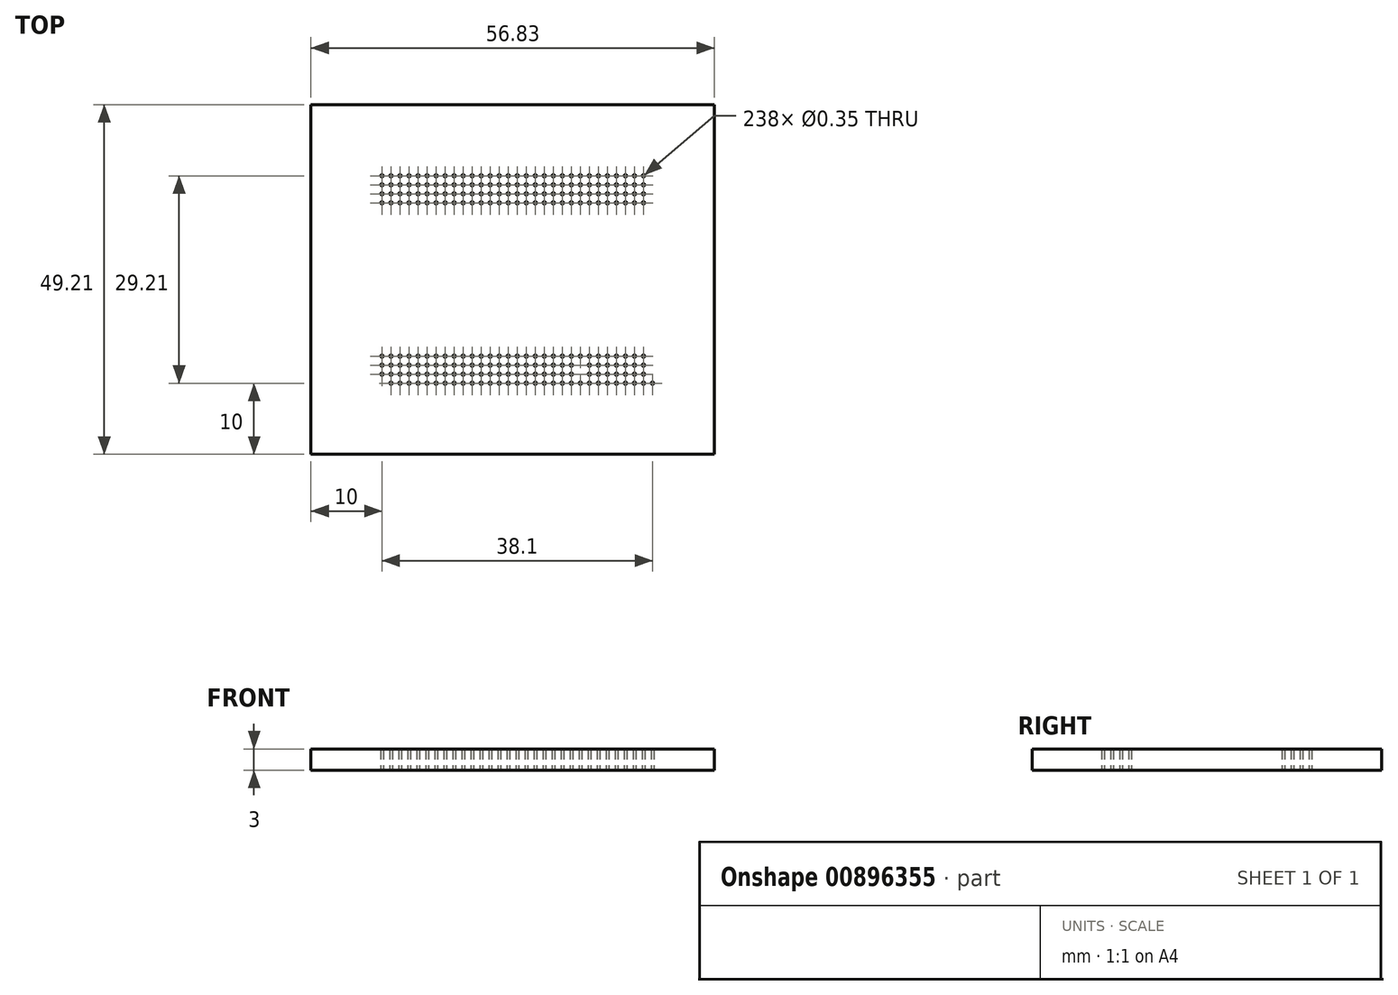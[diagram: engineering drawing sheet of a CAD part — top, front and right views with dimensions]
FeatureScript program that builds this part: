
annotation { "Feature Type Name" : "Feature", "Feature Type Description" : "" }
export const myFeature = defineFeature(function(context is Context, id is Id, definition is map)
    precondition{}
    {
        {
            var Q0;
            Q0=qCreatedBy(makeId("Top.planeOp"),FACE);
            var sketch = newSketch(context, id + "F0", { "sketchPlane" : qUnion([Q0])});
            skLineSegment(sketch, "E0.bottom", {"start": v(0, 0) * mm, "end": v(-56.83, 0) * mm});
            skLineSegment(sketch, "E0.top", {"start": v(0, 49.2) * mm, "end": v(-56.83, 49.2) * mm});
            skLineSegment(sketch, "E0.left", {"start": v(0, 0) * mm, "end": v(0, 49.2) * mm});
            skLineSegment(sketch, "E0.right", {"start": v(-56.83, 0) * mm, "end": v(-56.83, 49.2) * mm});
            skCircle(sketch, "E1", {"center": v(-46.83, 10) * mm, "radius": 0.18 * mm});
            skLineSegment(sketch, "E2", {"start": v(-46.83, 10) * mm, "end": v(-46.83, 10.4) * mm, "construction": true});
            skCircle(sketch, "E3", {"center": v(-46.83, 11.27) * mm, "radius": 0.17 * mm});
            skCircle(sketch, "E4", {"center": v(-46.83, 12.54) * mm, "radius": 0.17 * mm});
            skCircle(sketch, "E5", {"center": v(-46.83, 13.8) * mm, "radius": 0.17 * mm});
            skCircle(sketch, "E6.0.1.0", {"center": v(-46.83, 39.2) * mm, "radius": 0.17 * mm});
            skCircle(sketch, "E6.0.1.1", {"center": v(-46.83, 37.94) * mm, "radius": 0.17 * mm});
            skCircle(sketch, "E6.0.1.2", {"center": v(-46.83, 36.67) * mm, "radius": 0.17 * mm});
            skCircle(sketch, "E6.0.1.3", {"center": v(-46.83, 35.4) * mm, "radius": 0.18 * mm});
            skCircle(sketch, "E6.1.0.0", {"center": v(-45.56, 13.8) * mm, "radius": 0.17 * mm});
            skCircle(sketch, "E6.1.0.1", {"center": v(-45.56, 12.54) * mm, "radius": 0.17 * mm});
            skCircle(sketch, "E6.1.0.2", {"center": v(-45.56, 11.27) * mm, "radius": 0.17 * mm});
            skCircle(sketch, "E6.1.0.3", {"center": v(-45.56, 10) * mm, "radius": 0.18 * mm});
            skCircle(sketch, "E6.1.1.0", {"center": v(-45.56, 39.2) * mm, "radius": 0.17 * mm});
            skCircle(sketch, "E6.1.1.1", {"center": v(-45.56, 37.94) * mm, "radius": 0.17 * mm});
            skCircle(sketch, "E6.1.1.2", {"center": v(-45.56, 36.67) * mm, "radius": 0.17 * mm});
            skCircle(sketch, "E6.1.1.3", {"center": v(-45.56, 35.4) * mm, "radius": 0.18 * mm});
            skCircle(sketch, "E6.2.0.0", {"center": v(-44.3, 13.8) * mm, "radius": 0.17 * mm});
            skCircle(sketch, "E6.2.0.1", {"center": v(-44.3, 12.54) * mm, "radius": 0.17 * mm});
            skCircle(sketch, "E6.2.0.2", {"center": v(-44.3, 11.27) * mm, "radius": 0.17 * mm});
            skCircle(sketch, "E6.2.0.3", {"center": v(-44.3, 10) * mm, "radius": 0.18 * mm});
            skCircle(sketch, "E6.2.1.0", {"center": v(-44.3, 39.2) * mm, "radius": 0.17 * mm});
            skCircle(sketch, "E6.2.1.1", {"center": v(-44.3, 37.94) * mm, "radius": 0.17 * mm});
            skCircle(sketch, "E6.2.1.2", {"center": v(-44.3, 36.67) * mm, "radius": 0.17 * mm});
            skCircle(sketch, "E6.2.1.3", {"center": v(-44.3, 35.4) * mm, "radius": 0.18 * mm});
            skCircle(sketch, "E6.3.0.0", {"center": v(-43.02, 13.8) * mm, "radius": 0.17 * mm});
            skCircle(sketch, "E6.3.0.1", {"center": v(-43.02, 12.54) * mm, "radius": 0.17 * mm});
            skCircle(sketch, "E6.3.0.2", {"center": v(-43.02, 11.27) * mm, "radius": 0.17 * mm});
            skCircle(sketch, "E6.3.0.3", {"center": v(-43.02, 10) * mm, "radius": 0.18 * mm});
            skCircle(sketch, "E6.3.1.0", {"center": v(-43.02, 39.2) * mm, "radius": 0.17 * mm});
            skCircle(sketch, "E6.3.1.1", {"center": v(-43.02, 37.94) * mm, "radius": 0.17 * mm});
            skCircle(sketch, "E6.3.1.2", {"center": v(-43.02, 36.67) * mm, "radius": 0.17 * mm});
            skCircle(sketch, "E6.3.1.3", {"center": v(-43.02, 35.4) * mm, "radius": 0.18 * mm});
            skCircle(sketch, "E6.4.0.0", {"center": v(-41.75, 13.8) * mm, "radius": 0.17 * mm});
            skCircle(sketch, "E6.4.0.1", {"center": v(-41.75, 12.54) * mm, "radius": 0.17 * mm});
            skCircle(sketch, "E6.4.0.2", {"center": v(-41.75, 11.27) * mm, "radius": 0.17 * mm});
            skCircle(sketch, "E6.4.0.3", {"center": v(-41.75, 10) * mm, "radius": 0.18 * mm});
            skCircle(sketch, "E6.4.1.0", {"center": v(-41.75, 39.2) * mm, "radius": 0.17 * mm});
            skCircle(sketch, "E6.4.1.1", {"center": v(-41.75, 37.94) * mm, "radius": 0.17 * mm});
            skCircle(sketch, "E6.4.1.2", {"center": v(-41.75, 36.67) * mm, "radius": 0.17 * mm});
            skCircle(sketch, "E6.4.1.3", {"center": v(-41.75, 35.4) * mm, "radius": 0.18 * mm});
            skCircle(sketch, "E6.5.0.0", {"center": v(-40.48, 13.8) * mm, "radius": 0.17 * mm});
            skCircle(sketch, "E6.5.0.1", {"center": v(-40.48, 12.54) * mm, "radius": 0.17 * mm});
            skCircle(sketch, "E6.5.0.2", {"center": v(-40.48, 11.27) * mm, "radius": 0.17 * mm});
            skCircle(sketch, "E6.5.0.3", {"center": v(-40.48, 10) * mm, "radius": 0.18 * mm});
            skCircle(sketch, "E6.5.1.0", {"center": v(-40.48, 39.2) * mm, "radius": 0.17 * mm});
            skCircle(sketch, "E6.5.1.1", {"center": v(-40.48, 37.94) * mm, "radius": 0.17 * mm});
            skCircle(sketch, "E6.5.1.2", {"center": v(-40.48, 36.67) * mm, "radius": 0.17 * mm});
            skCircle(sketch, "E6.5.1.3", {"center": v(-40.48, 35.4) * mm, "radius": 0.18 * mm});
            skCircle(sketch, "E6.6.0.0", {"center": v(-39.21, 13.8) * mm, "radius": 0.17 * mm});
            skCircle(sketch, "E6.6.0.1", {"center": v(-39.21, 12.54) * mm, "radius": 0.17 * mm});
            skCircle(sketch, "E6.6.0.2", {"center": v(-39.21, 11.27) * mm, "radius": 0.17 * mm});
            skCircle(sketch, "E6.6.0.3", {"center": v(-39.21, 10) * mm, "radius": 0.18 * mm});
            skCircle(sketch, "E6.6.1.0", {"center": v(-39.21, 39.2) * mm, "radius": 0.17 * mm});
            skCircle(sketch, "E6.6.1.1", {"center": v(-39.21, 37.94) * mm, "radius": 0.17 * mm});
            skCircle(sketch, "E6.6.1.2", {"center": v(-39.21, 36.67) * mm, "radius": 0.17 * mm});
            skCircle(sketch, "E6.6.1.3", {"center": v(-39.21, 35.4) * mm, "radius": 0.18 * mm});
            skCircle(sketch, "E6.7.0.0", {"center": v(-37.94, 13.8) * mm, "radius": 0.17 * mm});
            skCircle(sketch, "E6.7.0.3", {"center": v(-37.94, 10) * mm, "radius": 0.18 * mm});
            skCircle(sketch, "E6.7.1.0", {"center": v(-37.94, 39.2) * mm, "radius": 0.17 * mm});
            skCircle(sketch, "E6.7.1.1", {"center": v(-37.94, 37.94) * mm, "radius": 0.17 * mm});
            skCircle(sketch, "E6.7.1.2", {"center": v(-37.94, 36.67) * mm, "radius": 0.17 * mm});
            skCircle(sketch, "E6.7.1.3", {"center": v(-37.94, 35.4) * mm, "radius": 0.18 * mm});
            skCircle(sketch, "E6.8.0.0", {"center": v(-36.67, 13.8) * mm, "radius": 0.17 * mm});
            skCircle(sketch, "E6.8.0.1", {"center": v(-36.67, 12.54) * mm, "radius": 0.17 * mm});
            skCircle(sketch, "E6.8.0.2", {"center": v(-36.67, 11.27) * mm, "radius": 0.17 * mm});
            skCircle(sketch, "E6.8.0.3", {"center": v(-36.67, 10) * mm, "radius": 0.18 * mm});
            skCircle(sketch, "E6.8.1.0", {"center": v(-36.67, 39.2) * mm, "radius": 0.17 * mm});
            skCircle(sketch, "E6.8.1.1", {"center": v(-36.67, 37.94) * mm, "radius": 0.17 * mm});
            skCircle(sketch, "E6.8.1.2", {"center": v(-36.67, 36.67) * mm, "radius": 0.17 * mm});
            skCircle(sketch, "E6.8.1.3", {"center": v(-36.67, 35.4) * mm, "radius": 0.18 * mm});
            skCircle(sketch, "E6.9.0.0", {"center": v(-35.4, 13.8) * mm, "radius": 0.17 * mm});
            skCircle(sketch, "E6.9.0.1", {"center": v(-35.4, 12.54) * mm, "radius": 0.17 * mm});
            skCircle(sketch, "E6.9.0.2", {"center": v(-35.4, 11.27) * mm, "radius": 0.17 * mm});
            skCircle(sketch, "E6.9.0.3", {"center": v(-35.4, 10) * mm, "radius": 0.18 * mm});
            skCircle(sketch, "E6.9.1.0", {"center": v(-35.4, 39.2) * mm, "radius": 0.17 * mm});
            skCircle(sketch, "E6.9.1.1", {"center": v(-35.4, 37.94) * mm, "radius": 0.17 * mm});
            skCircle(sketch, "E6.9.1.2", {"center": v(-35.4, 36.67) * mm, "radius": 0.17 * mm});
            skCircle(sketch, "E6.9.1.3", {"center": v(-35.4, 35.4) * mm, "radius": 0.18 * mm});
            skCircle(sketch, "E6.10.0.0", {"center": v(-34.13, 13.8) * mm, "radius": 0.17 * mm});
            skCircle(sketch, "E6.10.0.1", {"center": v(-34.13, 12.54) * mm, "radius": 0.17 * mm});
            skCircle(sketch, "E6.10.0.2", {"center": v(-34.13, 11.27) * mm, "radius": 0.17 * mm});
            skCircle(sketch, "E6.10.0.3", {"center": v(-34.13, 10) * mm, "radius": 0.18 * mm});
            skCircle(sketch, "E6.10.1.0", {"center": v(-34.13, 39.2) * mm, "radius": 0.17 * mm});
            skCircle(sketch, "E6.10.1.1", {"center": v(-34.13, 37.94) * mm, "radius": 0.17 * mm});
            skCircle(sketch, "E6.10.1.2", {"center": v(-34.13, 36.67) * mm, "radius": 0.17 * mm});
            skCircle(sketch, "E6.10.1.3", {"center": v(-34.13, 35.4) * mm, "radius": 0.18 * mm});
            skCircle(sketch, "E6.11.0.0", {"center": v(-32.86, 13.8) * mm, "radius": 0.17 * mm});
            skCircle(sketch, "E6.11.0.1", {"center": v(-32.86, 12.54) * mm, "radius": 0.17 * mm});
            skCircle(sketch, "E6.11.0.2", {"center": v(-32.86, 11.27) * mm, "radius": 0.17 * mm});
            skCircle(sketch, "E6.11.0.3", {"center": v(-32.86, 10) * mm, "radius": 0.18 * mm});
            skCircle(sketch, "E6.11.1.0", {"center": v(-32.86, 39.2) * mm, "radius": 0.17 * mm});
            skCircle(sketch, "E6.11.1.1", {"center": v(-32.86, 37.94) * mm, "radius": 0.17 * mm});
            skCircle(sketch, "E6.11.1.2", {"center": v(-32.86, 36.67) * mm, "radius": 0.17 * mm});
            skCircle(sketch, "E6.11.1.3", {"center": v(-32.86, 35.4) * mm, "radius": 0.18 * mm});
            skCircle(sketch, "E6.12.0.0", {"center": v(-31.6, 13.8) * mm, "radius": 0.17 * mm});
            skCircle(sketch, "E6.12.0.1", {"center": v(-31.6, 12.54) * mm, "radius": 0.17 * mm});
            skCircle(sketch, "E6.12.0.2", {"center": v(-31.6, 11.27) * mm, "radius": 0.17 * mm});
            skCircle(sketch, "E6.12.0.3", {"center": v(-31.6, 10) * mm, "radius": 0.18 * mm});
            skCircle(sketch, "E6.12.1.0", {"center": v(-31.6, 39.2) * mm, "radius": 0.17 * mm});
            skCircle(sketch, "E6.12.1.1", {"center": v(-31.6, 37.94) * mm, "radius": 0.17 * mm});
            skCircle(sketch, "E6.12.1.2", {"center": v(-31.6, 36.67) * mm, "radius": 0.17 * mm});
            skCircle(sketch, "E6.12.1.3", {"center": v(-31.6, 35.4) * mm, "radius": 0.18 * mm});
            skCircle(sketch, "E6.13.0.0", {"center": v(-30.32, 13.8) * mm, "radius": 0.17 * mm});
            skCircle(sketch, "E6.13.0.1", {"center": v(-30.32, 12.54) * mm, "radius": 0.17 * mm});
            skCircle(sketch, "E6.13.0.2", {"center": v(-30.32, 11.27) * mm, "radius": 0.17 * mm});
            skCircle(sketch, "E6.13.0.3", {"center": v(-30.32, 10) * mm, "radius": 0.18 * mm});
            skCircle(sketch, "E6.13.1.0", {"center": v(-30.32, 39.2) * mm, "radius": 0.17 * mm});
            skCircle(sketch, "E6.13.1.1", {"center": v(-30.32, 37.94) * mm, "radius": 0.17 * mm});
            skCircle(sketch, "E6.13.1.2", {"center": v(-30.32, 36.67) * mm, "radius": 0.17 * mm});
            skCircle(sketch, "E6.13.1.3", {"center": v(-30.32, 35.4) * mm, "radius": 0.18 * mm});
            skCircle(sketch, "E6.14.0.0", {"center": v(-29.05, 13.8) * mm, "radius": 0.17 * mm});
            skCircle(sketch, "E6.14.0.1", {"center": v(-29.05, 12.54) * mm, "radius": 0.17 * mm});
            skCircle(sketch, "E6.14.0.2", {"center": v(-29.05, 11.27) * mm, "radius": 0.17 * mm});
            skCircle(sketch, "E6.14.0.3", {"center": v(-29.05, 10) * mm, "radius": 0.18 * mm});
            skCircle(sketch, "E6.14.1.0", {"center": v(-29.05, 39.2) * mm, "radius": 0.17 * mm});
            skCircle(sketch, "E6.14.1.1", {"center": v(-29.05, 37.94) * mm, "radius": 0.17 * mm});
            skCircle(sketch, "E6.14.1.2", {"center": v(-29.05, 36.67) * mm, "radius": 0.17 * mm});
            skCircle(sketch, "E6.14.1.3", {"center": v(-29.05, 35.4) * mm, "radius": 0.18 * mm});
            skCircle(sketch, "E6.15.0.0", {"center": v(-27.78, 13.8) * mm, "radius": 0.17 * mm});
            skCircle(sketch, "E6.15.0.1", {"center": v(-27.78, 12.54) * mm, "radius": 0.17 * mm});
            skCircle(sketch, "E6.15.0.2", {"center": v(-27.78, 11.27) * mm, "radius": 0.17 * mm});
            skCircle(sketch, "E6.15.0.3", {"center": v(-27.78, 10) * mm, "radius": 0.18 * mm});
            skCircle(sketch, "E6.15.1.0", {"center": v(-27.78, 39.2) * mm, "radius": 0.17 * mm});
            skCircle(sketch, "E6.15.1.1", {"center": v(-27.78, 37.94) * mm, "radius": 0.17 * mm});
            skCircle(sketch, "E6.15.1.2", {"center": v(-27.78, 36.67) * mm, "radius": 0.17 * mm});
            skCircle(sketch, "E6.15.1.3", {"center": v(-27.78, 35.4) * mm, "radius": 0.18 * mm});
            skCircle(sketch, "E6.16.0.0", {"center": v(-26.51, 13.8) * mm, "radius": 0.17 * mm});
            skCircle(sketch, "E6.16.0.1", {"center": v(-26.51, 12.54) * mm, "radius": 0.17 * mm});
            skCircle(sketch, "E6.16.0.2", {"center": v(-26.51, 11.27) * mm, "radius": 0.17 * mm});
            skCircle(sketch, "E6.16.0.3", {"center": v(-26.51, 10) * mm, "radius": 0.18 * mm});
            skCircle(sketch, "E6.16.1.0", {"center": v(-26.51, 39.2) * mm, "radius": 0.17 * mm});
            skCircle(sketch, "E6.16.1.1", {"center": v(-26.51, 37.94) * mm, "radius": 0.17 * mm});
            skCircle(sketch, "E6.16.1.2", {"center": v(-26.51, 36.67) * mm, "radius": 0.17 * mm});
            skCircle(sketch, "E6.16.1.3", {"center": v(-26.51, 35.4) * mm, "radius": 0.18 * mm});
            skCircle(sketch, "E6.17.0.0", {"center": v(-25.24, 13.8) * mm, "radius": 0.17 * mm});
            skCircle(sketch, "E6.17.0.1", {"center": v(-25.24, 12.54) * mm, "radius": 0.17 * mm});
            skCircle(sketch, "E6.17.0.2", {"center": v(-25.24, 11.27) * mm, "radius": 0.17 * mm});
            skCircle(sketch, "E6.17.0.3", {"center": v(-25.24, 10) * mm, "radius": 0.18 * mm});
            skCircle(sketch, "E6.17.1.0", {"center": v(-25.24, 39.2) * mm, "radius": 0.17 * mm});
            skCircle(sketch, "E6.17.1.1", {"center": v(-25.24, 37.94) * mm, "radius": 0.17 * mm});
            skCircle(sketch, "E6.17.1.2", {"center": v(-25.24, 36.67) * mm, "radius": 0.17 * mm});
            skCircle(sketch, "E6.17.1.3", {"center": v(-25.24, 35.4) * mm, "radius": 0.18 * mm});
            skCircle(sketch, "E6.18.0.0", {"center": v(-23.97, 13.8) * mm, "radius": 0.17 * mm});
            skCircle(sketch, "E6.18.0.1", {"center": v(-23.97, 12.54) * mm, "radius": 0.17 * mm});
            skCircle(sketch, "E6.18.0.2", {"center": v(-23.97, 11.27) * mm, "radius": 0.17 * mm});
            skCircle(sketch, "E6.18.0.3", {"center": v(-23.97, 10) * mm, "radius": 0.18 * mm});
            skCircle(sketch, "E6.18.1.0", {"center": v(-23.97, 39.2) * mm, "radius": 0.17 * mm});
            skCircle(sketch, "E6.18.1.1", {"center": v(-23.97, 37.94) * mm, "radius": 0.17 * mm});
            skCircle(sketch, "E6.18.1.2", {"center": v(-23.97, 36.67) * mm, "radius": 0.17 * mm});
            skCircle(sketch, "E6.18.1.3", {"center": v(-23.97, 35.4) * mm, "radius": 0.18 * mm});
            skCircle(sketch, "E6.19.0.0", {"center": v(-22.7, 13.8) * mm, "radius": 0.17 * mm});
            skCircle(sketch, "E6.19.0.1", {"center": v(-22.7, 12.54) * mm, "radius": 0.17 * mm});
            skCircle(sketch, "E6.19.0.2", {"center": v(-22.7, 11.27) * mm, "radius": 0.17 * mm});
            skCircle(sketch, "E6.19.0.3", {"center": v(-22.7, 10) * mm, "radius": 0.18 * mm});
            skCircle(sketch, "E6.19.1.0", {"center": v(-22.7, 39.2) * mm, "radius": 0.17 * mm});
            skCircle(sketch, "E6.19.1.1", {"center": v(-22.7, 37.94) * mm, "radius": 0.17 * mm});
            skCircle(sketch, "E6.19.1.2", {"center": v(-22.7, 36.67) * mm, "radius": 0.17 * mm});
            skCircle(sketch, "E6.19.1.3", {"center": v(-22.7, 35.4) * mm, "radius": 0.18 * mm});
            skCircle(sketch, "E6.20.0.0", {"center": v(-21.43, 13.8) * mm, "radius": 0.17 * mm});
            skCircle(sketch, "E6.20.0.1", {"center": v(-21.43, 12.54) * mm, "radius": 0.17 * mm});
            skCircle(sketch, "E6.20.0.2", {"center": v(-21.43, 11.27) * mm, "radius": 0.17 * mm});
            skCircle(sketch, "E6.20.0.3", {"center": v(-21.43, 10) * mm, "radius": 0.18 * mm});
            skCircle(sketch, "E6.20.1.0", {"center": v(-21.43, 39.2) * mm, "radius": 0.17 * mm});
            skCircle(sketch, "E6.20.1.1", {"center": v(-21.43, 37.94) * mm, "radius": 0.17 * mm});
            skCircle(sketch, "E6.20.1.2", {"center": v(-21.43, 36.67) * mm, "radius": 0.17 * mm});
            skCircle(sketch, "E6.20.1.3", {"center": v(-21.43, 35.4) * mm, "radius": 0.18 * mm});
            skCircle(sketch, "E6.21.0.0", {"center": v(-20.16, 13.8) * mm, "radius": 0.17 * mm});
            skCircle(sketch, "E6.21.0.1", {"center": v(-20.16, 12.54) * mm, "radius": 0.17 * mm});
            skCircle(sketch, "E6.21.0.2", {"center": v(-20.16, 11.27) * mm, "radius": 0.17 * mm});
            skCircle(sketch, "E6.21.0.3", {"center": v(-20.16, 10) * mm, "radius": 0.18 * mm});
            skCircle(sketch, "E6.21.1.0", {"center": v(-20.16, 39.2) * mm, "radius": 0.17 * mm});
            skCircle(sketch, "E6.21.1.1", {"center": v(-20.16, 37.94) * mm, "radius": 0.17 * mm});
            skCircle(sketch, "E6.21.1.2", {"center": v(-20.16, 36.67) * mm, "radius": 0.17 * mm});
            skCircle(sketch, "E6.21.1.3", {"center": v(-20.16, 35.4) * mm, "radius": 0.18 * mm});
            skCircle(sketch, "E6.22.0.0", {"center": v(-18.9, 13.8) * mm, "radius": 0.17 * mm});
            skCircle(sketch, "E6.22.0.1", {"center": v(-18.9, 12.54) * mm, "radius": 0.17 * mm});
            skCircle(sketch, "E6.22.0.2", {"center": v(-18.9, 11.27) * mm, "radius": 0.17 * mm});
            skCircle(sketch, "E6.22.0.3", {"center": v(-18.9, 10) * mm, "radius": 0.18 * mm});
            skCircle(sketch, "E6.22.1.0", {"center": v(-18.9, 39.2) * mm, "radius": 0.17 * mm});
            skCircle(sketch, "E6.22.1.1", {"center": v(-18.9, 37.94) * mm, "radius": 0.17 * mm});
            skCircle(sketch, "E6.22.1.2", {"center": v(-18.9, 36.67) * mm, "radius": 0.17 * mm});
            skCircle(sketch, "E6.22.1.3", {"center": v(-18.9, 35.4) * mm, "radius": 0.18 * mm});
            skCircle(sketch, "E6.23.0.0", {"center": v(-17.62, 13.8) * mm, "radius": 0.17 * mm});
            skCircle(sketch, "E6.23.0.1", {"center": v(-17.62, 12.54) * mm, "radius": 0.17 * mm});
            skCircle(sketch, "E6.23.0.2", {"center": v(-17.62, 11.27) * mm, "radius": 0.17 * mm});
            skCircle(sketch, "E6.23.0.3", {"center": v(-17.62, 10) * mm, "radius": 0.18 * mm});
            skCircle(sketch, "E6.23.1.0", {"center": v(-17.62, 39.2) * mm, "radius": 0.17 * mm});
            skCircle(sketch, "E6.23.1.1", {"center": v(-17.62, 37.94) * mm, "radius": 0.17 * mm});
            skCircle(sketch, "E6.23.1.2", {"center": v(-17.62, 36.67) * mm, "radius": 0.17 * mm});
            skCircle(sketch, "E6.23.1.3", {"center": v(-17.62, 35.4) * mm, "radius": 0.18 * mm});
            skCircle(sketch, "E6.24.0.0", {"center": v(-16.35, 13.8) * mm, "radius": 0.17 * mm});
            skCircle(sketch, "E6.24.0.1", {"center": v(-16.35, 12.54) * mm, "radius": 0.17 * mm});
            skCircle(sketch, "E6.24.0.2", {"center": v(-16.35, 11.27) * mm, "radius": 0.17 * mm});
            skCircle(sketch, "E6.24.0.3", {"center": v(-16.35, 10) * mm, "radius": 0.18 * mm});
            skCircle(sketch, "E6.24.1.0", {"center": v(-16.35, 39.2) * mm, "radius": 0.17 * mm});
            skCircle(sketch, "E6.24.1.1", {"center": v(-16.35, 37.94) * mm, "radius": 0.17 * mm});
            skCircle(sketch, "E6.24.1.2", {"center": v(-16.35, 36.67) * mm, "radius": 0.17 * mm});
            skCircle(sketch, "E6.24.1.3", {"center": v(-16.35, 35.4) * mm, "radius": 0.18 * mm});
            skCircle(sketch, "E6.25.0.0", {"center": v(-15.08, 13.8) * mm, "radius": 0.17 * mm});
            skCircle(sketch, "E6.25.0.1", {"center": v(-15.08, 12.54) * mm, "radius": 0.17 * mm});
            skCircle(sketch, "E6.25.0.2", {"center": v(-15.08, 11.27) * mm, "radius": 0.17 * mm});
            skCircle(sketch, "E6.25.0.3", {"center": v(-15.08, 10) * mm, "radius": 0.18 * mm});
            skCircle(sketch, "E6.25.1.0", {"center": v(-15.08, 39.2) * mm, "radius": 0.17 * mm});
            skCircle(sketch, "E6.25.1.1", {"center": v(-15.08, 37.94) * mm, "radius": 0.17 * mm});
            skCircle(sketch, "E6.25.1.2", {"center": v(-15.08, 36.67) * mm, "radius": 0.17 * mm});
            skCircle(sketch, "E6.25.1.3", {"center": v(-15.08, 35.4) * mm, "radius": 0.18 * mm});
            skCircle(sketch, "E6.26.0.0", {"center": v(-13.81, 13.8) * mm, "radius": 0.17 * mm});
            skCircle(sketch, "E6.26.0.1", {"center": v(-13.81, 12.54) * mm, "radius": 0.17 * mm});
            skCircle(sketch, "E6.26.0.2", {"center": v(-13.81, 11.27) * mm, "radius": 0.17 * mm});
            skCircle(sketch, "E6.26.0.3", {"center": v(-13.81, 10) * mm, "radius": 0.18 * mm});
            skCircle(sketch, "E6.26.1.0", {"center": v(-13.81, 39.2) * mm, "radius": 0.17 * mm});
            skCircle(sketch, "E6.26.1.1", {"center": v(-13.81, 37.94) * mm, "radius": 0.17 * mm});
            skCircle(sketch, "E6.26.1.2", {"center": v(-13.81, 36.67) * mm, "radius": 0.17 * mm});
            skCircle(sketch, "E6.26.1.3", {"center": v(-13.81, 35.4) * mm, "radius": 0.18 * mm});
            skCircle(sketch, "E6.27.0.0", {"center": v(-12.54, 13.8) * mm, "radius": 0.17 * mm});
            skCircle(sketch, "E6.27.0.1", {"center": v(-12.54, 12.54) * mm, "radius": 0.17 * mm});
            skCircle(sketch, "E6.27.0.2", {"center": v(-12.54, 11.27) * mm, "radius": 0.17 * mm});
            skCircle(sketch, "E6.27.0.3", {"center": v(-12.54, 10) * mm, "radius": 0.18 * mm});
            skCircle(sketch, "E6.27.1.0", {"center": v(-12.54, 39.2) * mm, "radius": 0.17 * mm});
            skCircle(sketch, "E6.27.1.1", {"center": v(-12.54, 37.94) * mm, "radius": 0.17 * mm});
            skCircle(sketch, "E6.27.1.2", {"center": v(-12.54, 36.67) * mm, "radius": 0.17 * mm});
            skCircle(sketch, "E6.27.1.3", {"center": v(-12.54, 35.4) * mm, "radius": 0.18 * mm});
            skCircle(sketch, "E6.28.0.0", {"center": v(-11.27, 13.8) * mm, "radius": 0.17 * mm});
            skCircle(sketch, "E6.28.0.1", {"center": v(-11.27, 12.54) * mm, "radius": 0.17 * mm});
            skCircle(sketch, "E6.28.0.2", {"center": v(-11.27, 11.27) * mm, "radius": 0.17 * mm});
            skCircle(sketch, "E6.28.0.3", {"center": v(-11.27, 10) * mm, "radius": 0.18 * mm});
            skCircle(sketch, "E6.28.1.0", {"center": v(-11.27, 39.2) * mm, "radius": 0.17 * mm});
            skCircle(sketch, "E6.28.1.1", {"center": v(-11.27, 37.94) * mm, "radius": 0.17 * mm});
            skCircle(sketch, "E6.28.1.2", {"center": v(-11.27, 36.67) * mm, "radius": 0.17 * mm});
            skCircle(sketch, "E6.28.1.3", {"center": v(-11.27, 35.4) * mm, "radius": 0.18 * mm});
            skCircle(sketch, "E6.29.0.0", {"center": v(-10, 13.8) * mm, "radius": 0.17 * mm});
            skCircle(sketch, "E6.29.0.1", {"center": v(-10, 12.54) * mm, "radius": 0.17 * mm});
            skCircle(sketch, "E6.29.0.2", {"center": v(-10, 11.27) * mm, "radius": 0.17 * mm});
            skCircle(sketch, "E6.29.1.0", {"center": v(-10, 39.2) * mm, "radius": 0.17 * mm});
            skCircle(sketch, "E6.29.1.1", {"center": v(-10, 37.94) * mm, "radius": 0.17 * mm});
            skCircle(sketch, "E6.29.1.2", {"center": v(-10, 36.67) * mm, "radius": 0.17 * mm});
            skCircle(sketch, "E6.29.1.3", {"center": v(-10, 35.4) * mm, "radius": 0.18 * mm});
            skLineSegment(sketch, "E6.direction1", {"start": v(-46.83, 13.8) * mm, "end": v(-45.56, 13.8) * mm, "construction": true});
            skLineSegment(sketch, "E6.direction2", {"start": v(-46.83, 13.8) * mm, "end": v(-46.83, 39.2) * mm, "construction": true});
            skCircle(sketch, "E7", {"center": v(-48.1, 10) * mm, "radius": 0.17 * mm});
            skLineSegment(sketch, "E8", {"start": v(-44.97, 10) * mm, "end": v(-46.83, 10) * mm, "construction": true});
            skSolve(sketch);
        }
        {
            var Q0;
            Q0=makeQuery(id+"F0.imprint","IMPRINT",FACE,{"disambiguationData":[TD([[makeQuery(id+"F0.imprint","IMPRINT",EDGE,{"derivedFrom":sQuery(id+"F0.wireOp",EDGE,"E0.bottom")}),-1.0]])]});
            extrude(context, id + "F1", {"entities" : qUnion([Q0]), "depth" : 3 * mm, "offsetDistance" : 25 * mm});
        }
        {
            var Q0;
            Q0=makeQuery(id+"F1.opExtrude","SWEPT_BODY",BODY,{"disambiguationData":[OSD([sQuery(id+"F0.wireOp",EDGE,"E0.bottom"),sQuery(id+"F0.wireOp",EDGE,"E0.top"),sQuery(id+"F0.wireOp",EDGE,"E0.left"),sQuery(id+"F0.wireOp",EDGE,"E0.right"),sQuery(id+"F0.wireOp",EDGE,"E1"),sQuery(id+"F0.wireOp",EDGE,"E3"),sQuery(id+"F0.wireOp",EDGE,"E4"),sQuery(id+"F0.wireOp",EDGE,"E5"),sQuery(id+"F0.wireOp",EDGE,"E6.0.1.0"),sQuery(id+"F0.wireOp",EDGE,"E6.0.1.1"),sQuery(id+"F0.wireOp",EDGE,"E6.0.1.2"),sQuery(id+"F0.wireOp",EDGE,"E6.0.1.3"),sQuery(id+"F0.wireOp",EDGE,"E6.1.0.0"),sQuery(id+"F0.wireOp",EDGE,"E6.1.0.1"),sQuery(id+"F0.wireOp",EDGE,"E6.1.0.2"),sQuery(id+"F0.wireOp",EDGE,"E6.1.0.3"),sQuery(id+"F0.wireOp",EDGE,"E6.1.1.0"),sQuery(id+"F0.wireOp",EDGE,"E6.1.1.1"),sQuery(id+"F0.wireOp",EDGE,"E6.1.1.2"),sQuery(id+"F0.wireOp",EDGE,"E6.1.1.3"),sQuery(id+"F0.wireOp",EDGE,"E6.2.0.0"),sQuery(id+"F0.wireOp",EDGE,"E6.2.0.1"),sQuery(id+"F0.wireOp",EDGE,"E6.2.0.2"),sQuery(id+"F0.wireOp",EDGE,"E6.2.0.3"),sQuery(id+"F0.wireOp",EDGE,"E6.2.1.0"),sQuery(id+"F0.wireOp",EDGE,"E6.2.1.1"),sQuery(id+"F0.wireOp",EDGE,"E6.2.1.2"),sQuery(id+"F0.wireOp",EDGE,"E6.2.1.3"),sQuery(id+"F0.wireOp",EDGE,"E6.3.0.0"),sQuery(id+"F0.wireOp",EDGE,"E6.3.0.1"),sQuery(id+"F0.wireOp",EDGE,"E6.3.0.2"),sQuery(id+"F0.wireOp",EDGE,"E6.3.0.3"),sQuery(id+"F0.wireOp",EDGE,"E6.3.1.0"),sQuery(id+"F0.wireOp",EDGE,"E6.3.1.1"),sQuery(id+"F0.wireOp",EDGE,"E6.3.1.2"),sQuery(id+"F0.wireOp",EDGE,"E6.3.1.3"),sQuery(id+"F0.wireOp",EDGE,"E6.4.0.0"),sQuery(id+"F0.wireOp",EDGE,"E6.4.0.1"),sQuery(id+"F0.wireOp",EDGE,"E6.4.0.2"),sQuery(id+"F0.wireOp",EDGE,"E6.4.0.3"),sQuery(id+"F0.wireOp",EDGE,"E6.4.1.0"),sQuery(id+"F0.wireOp",EDGE,"E6.4.1.1"),sQuery(id+"F0.wireOp",EDGE,"E6.4.1.2"),sQuery(id+"F0.wireOp",EDGE,"E6.4.1.3"),sQuery(id+"F0.wireOp",EDGE,"E6.5.0.0"),sQuery(id+"F0.wireOp",EDGE,"E6.5.0.1"),sQuery(id+"F0.wireOp",EDGE,"E6.5.0.2"),sQuery(id+"F0.wireOp",EDGE,"E6.5.0.3"),sQuery(id+"F0.wireOp",EDGE,"E6.5.1.0"),sQuery(id+"F0.wireOp",EDGE,"E6.5.1.1"),sQuery(id+"F0.wireOp",EDGE,"E6.5.1.2"),sQuery(id+"F0.wireOp",EDGE,"E6.5.1.3"),sQuery(id+"F0.wireOp",EDGE,"E6.6.0.0"),sQuery(id+"F0.wireOp",EDGE,"E6.6.0.1"),sQuery(id+"F0.wireOp",EDGE,"E6.6.0.2"),sQuery(id+"F0.wireOp",EDGE,"E6.6.0.3"),sQuery(id+"F0.wireOp",EDGE,"E6.6.1.0"),sQuery(id+"F0.wireOp",EDGE,"E6.6.1.1"),sQuery(id+"F0.wireOp",EDGE,"E6.6.1.2"),sQuery(id+"F0.wireOp",EDGE,"E6.6.1.3"),sQuery(id+"F0.wireOp",EDGE,"E6.7.0.0"),sQuery(id+"F0.wireOp",EDGE,"E6.7.0.3"),sQuery(id+"F0.wireOp",EDGE,"E6.7.1.0"),sQuery(id+"F0.wireOp",EDGE,"E6.7.1.1"),sQuery(id+"F0.wireOp",EDGE,"E6.7.1.2"),sQuery(id+"F0.wireOp",EDGE,"E6.7.1.3"),sQuery(id+"F0.wireOp",EDGE,"E6.8.0.0"),sQuery(id+"F0.wireOp",EDGE,"E6.8.0.1"),sQuery(id+"F0.wireOp",EDGE,"E6.8.0.2"),sQuery(id+"F0.wireOp",EDGE,"E6.8.0.3"),sQuery(id+"F0.wireOp",EDGE,"E6.8.1.0"),sQuery(id+"F0.wireOp",EDGE,"E6.8.1.1"),sQuery(id+"F0.wireOp",EDGE,"E6.8.1.2"),sQuery(id+"F0.wireOp",EDGE,"E6.8.1.3"),sQuery(id+"F0.wireOp",EDGE,"E6.9.0.0"),sQuery(id+"F0.wireOp",EDGE,"E6.9.0.1"),sQuery(id+"F0.wireOp",EDGE,"E6.9.0.2"),sQuery(id+"F0.wireOp",EDGE,"E6.9.0.3"),sQuery(id+"F0.wireOp",EDGE,"E6.9.1.0"),sQuery(id+"F0.wireOp",EDGE,"E6.9.1.1"),sQuery(id+"F0.wireOp",EDGE,"E6.9.1.2"),sQuery(id+"F0.wireOp",EDGE,"E6.9.1.3"),sQuery(id+"F0.wireOp",EDGE,"E6.10.0.0"),sQuery(id+"F0.wireOp",EDGE,"E6.10.0.1"),sQuery(id+"F0.wireOp",EDGE,"E6.10.0.2"),sQuery(id+"F0.wireOp",EDGE,"E6.10.0.3"),sQuery(id+"F0.wireOp",EDGE,"E6.10.1.0"),sQuery(id+"F0.wireOp",EDGE,"E6.10.1.1"),sQuery(id+"F0.wireOp",EDGE,"E6.10.1.2"),sQuery(id+"F0.wireOp",EDGE,"E6.10.1.3"),sQuery(id+"F0.wireOp",EDGE,"E6.11.0.0"),sQuery(id+"F0.wireOp",EDGE,"E6.11.0.1"),sQuery(id+"F0.wireOp",EDGE,"E6.11.0.2"),sQuery(id+"F0.wireOp",EDGE,"E6.11.0.3"),sQuery(id+"F0.wireOp",EDGE,"E6.11.1.0"),sQuery(id+"F0.wireOp",EDGE,"E6.11.1.1"),sQuery(id+"F0.wireOp",EDGE,"E6.11.1.2"),sQuery(id+"F0.wireOp",EDGE,"E6.11.1.3"),sQuery(id+"F0.wireOp",EDGE,"E6.12.0.0"),sQuery(id+"F0.wireOp",EDGE,"E6.12.0.1"),sQuery(id+"F0.wireOp",EDGE,"E6.12.0.2"),sQuery(id+"F0.wireOp",EDGE,"E6.12.0.3"),sQuery(id+"F0.wireOp",EDGE,"E6.12.1.0"),sQuery(id+"F0.wireOp",EDGE,"E6.12.1.1"),sQuery(id+"F0.wireOp",EDGE,"E6.12.1.2"),sQuery(id+"F0.wireOp",EDGE,"E6.12.1.3"),sQuery(id+"F0.wireOp",EDGE,"E6.13.0.0"),sQuery(id+"F0.wireOp",EDGE,"E6.13.0.1"),sQuery(id+"F0.wireOp",EDGE,"E6.13.0.2"),sQuery(id+"F0.wireOp",EDGE,"E6.13.0.3"),sQuery(id+"F0.wireOp",EDGE,"E6.13.1.0"),sQuery(id+"F0.wireOp",EDGE,"E6.13.1.1"),sQuery(id+"F0.wireOp",EDGE,"E6.13.1.2"),sQuery(id+"F0.wireOp",EDGE,"E6.13.1.3"),sQuery(id+"F0.wireOp",EDGE,"E6.14.0.0"),sQuery(id+"F0.wireOp",EDGE,"E6.14.0.1"),sQuery(id+"F0.wireOp",EDGE,"E6.14.0.2"),sQuery(id+"F0.wireOp",EDGE,"E6.14.0.3"),sQuery(id+"F0.wireOp",EDGE,"E6.14.1.0"),sQuery(id+"F0.wireOp",EDGE,"E6.14.1.1"),sQuery(id+"F0.wireOp",EDGE,"E6.14.1.2"),sQuery(id+"F0.wireOp",EDGE,"E6.14.1.3"),sQuery(id+"F0.wireOp",EDGE,"E6.15.0.0"),sQuery(id+"F0.wireOp",EDGE,"E6.15.0.1"),sQuery(id+"F0.wireOp",EDGE,"E6.15.0.2"),sQuery(id+"F0.wireOp",EDGE,"E6.15.0.3"),sQuery(id+"F0.wireOp",EDGE,"E6.15.1.0"),sQuery(id+"F0.wireOp",EDGE,"E6.15.1.1"),sQuery(id+"F0.wireOp",EDGE,"E6.15.1.2"),sQuery(id+"F0.wireOp",EDGE,"E6.15.1.3"),sQuery(id+"F0.wireOp",EDGE,"E6.16.0.0"),sQuery(id+"F0.wireOp",EDGE,"E6.16.0.1"),sQuery(id+"F0.wireOp",EDGE,"E6.16.0.2"),sQuery(id+"F0.wireOp",EDGE,"E6.16.0.3"),sQuery(id+"F0.wireOp",EDGE,"E6.16.1.0"),sQuery(id+"F0.wireOp",EDGE,"E6.16.1.1"),sQuery(id+"F0.wireOp",EDGE,"E6.16.1.2"),sQuery(id+"F0.wireOp",EDGE,"E6.16.1.3"),sQuery(id+"F0.wireOp",EDGE,"E6.17.0.0"),sQuery(id+"F0.wireOp",EDGE,"E6.17.0.1"),sQuery(id+"F0.wireOp",EDGE,"E6.17.0.2"),sQuery(id+"F0.wireOp",EDGE,"E6.17.0.3"),sQuery(id+"F0.wireOp",EDGE,"E6.17.1.0"),sQuery(id+"F0.wireOp",EDGE,"E6.17.1.1"),sQuery(id+"F0.wireOp",EDGE,"E6.17.1.2"),sQuery(id+"F0.wireOp",EDGE,"E6.17.1.3"),sQuery(id+"F0.wireOp",EDGE,"E6.18.0.0"),sQuery(id+"F0.wireOp",EDGE,"E6.18.0.1"),sQuery(id+"F0.wireOp",EDGE,"E6.18.0.2"),sQuery(id+"F0.wireOp",EDGE,"E6.18.0.3"),sQuery(id+"F0.wireOp",EDGE,"E6.18.1.0"),sQuery(id+"F0.wireOp",EDGE,"E6.18.1.1"),sQuery(id+"F0.wireOp",EDGE,"E6.18.1.2"),sQuery(id+"F0.wireOp",EDGE,"E6.18.1.3"),sQuery(id+"F0.wireOp",EDGE,"E6.19.0.0"),sQuery(id+"F0.wireOp",EDGE,"E6.19.0.1"),sQuery(id+"F0.wireOp",EDGE,"E6.19.0.2"),sQuery(id+"F0.wireOp",EDGE,"E6.19.0.3"),sQuery(id+"F0.wireOp",EDGE,"E6.19.1.0"),sQuery(id+"F0.wireOp",EDGE,"E6.19.1.1"),sQuery(id+"F0.wireOp",EDGE,"E6.19.1.2"),sQuery(id+"F0.wireOp",EDGE,"E6.19.1.3"),sQuery(id+"F0.wireOp",EDGE,"E6.20.0.0"),sQuery(id+"F0.wireOp",EDGE,"E6.20.0.1"),sQuery(id+"F0.wireOp",EDGE,"E6.20.0.2"),sQuery(id+"F0.wireOp",EDGE,"E6.20.0.3"),sQuery(id+"F0.wireOp",EDGE,"E6.20.1.0"),sQuery(id+"F0.wireOp",EDGE,"E6.20.1.1"),sQuery(id+"F0.wireOp",EDGE,"E6.20.1.2"),sQuery(id+"F0.wireOp",EDGE,"E6.20.1.3"),sQuery(id+"F0.wireOp",EDGE,"E6.21.0.0"),sQuery(id+"F0.wireOp",EDGE,"E6.21.0.1"),sQuery(id+"F0.wireOp",EDGE,"E6.21.0.2"),sQuery(id+"F0.wireOp",EDGE,"E6.21.0.3"),sQuery(id+"F0.wireOp",EDGE,"E6.21.1.0"),sQuery(id+"F0.wireOp",EDGE,"E6.21.1.1"),sQuery(id+"F0.wireOp",EDGE,"E6.21.1.2"),sQuery(id+"F0.wireOp",EDGE,"E6.21.1.3"),sQuery(id+"F0.wireOp",EDGE,"E6.22.0.0"),sQuery(id+"F0.wireOp",EDGE,"E6.22.0.1"),sQuery(id+"F0.wireOp",EDGE,"E6.22.0.2"),sQuery(id+"F0.wireOp",EDGE,"E6.22.0.3"),sQuery(id+"F0.wireOp",EDGE,"E6.22.1.0"),sQuery(id+"F0.wireOp",EDGE,"E6.22.1.1"),sQuery(id+"F0.wireOp",EDGE,"E6.22.1.2"),sQuery(id+"F0.wireOp",EDGE,"E6.22.1.3"),sQuery(id+"F0.wireOp",EDGE,"E6.23.0.0"),sQuery(id+"F0.wireOp",EDGE,"E6.23.0.1"),sQuery(id+"F0.wireOp",EDGE,"E6.23.0.2"),sQuery(id+"F0.wireOp",EDGE,"E6.23.0.3"),sQuery(id+"F0.wireOp",EDGE,"E6.23.1.0"),sQuery(id+"F0.wireOp",EDGE,"E6.23.1.1"),sQuery(id+"F0.wireOp",EDGE,"E6.23.1.2"),sQuery(id+"F0.wireOp",EDGE,"E6.23.1.3"),sQuery(id+"F0.wireOp",EDGE,"E6.24.0.0"),sQuery(id+"F0.wireOp",EDGE,"E6.24.0.1"),sQuery(id+"F0.wireOp",EDGE,"E6.24.0.2"),sQuery(id+"F0.wireOp",EDGE,"E6.24.0.3"),sQuery(id+"F0.wireOp",EDGE,"E6.24.1.0"),sQuery(id+"F0.wireOp",EDGE,"E6.24.1.1"),sQuery(id+"F0.wireOp",EDGE,"E6.24.1.2"),sQuery(id+"F0.wireOp",EDGE,"E6.24.1.3"),sQuery(id+"F0.wireOp",EDGE,"E6.25.0.0"),sQuery(id+"F0.wireOp",EDGE,"E6.25.0.1"),sQuery(id+"F0.wireOp",EDGE,"E6.25.0.2"),sQuery(id+"F0.wireOp",EDGE,"E6.25.0.3"),sQuery(id+"F0.wireOp",EDGE,"E6.25.1.0"),sQuery(id+"F0.wireOp",EDGE,"E6.25.1.1"),sQuery(id+"F0.wireOp",EDGE,"E6.25.1.2"),sQuery(id+"F0.wireOp",EDGE,"E6.25.1.3"),sQuery(id+"F0.wireOp",EDGE,"E6.26.0.0"),sQuery(id+"F0.wireOp",EDGE,"E6.26.0.1"),sQuery(id+"F0.wireOp",EDGE,"E6.26.0.2"),sQuery(id+"F0.wireOp",EDGE,"E6.26.0.3"),sQuery(id+"F0.wireOp",EDGE,"E6.26.1.0"),sQuery(id+"F0.wireOp",EDGE,"E6.26.1.1"),sQuery(id+"F0.wireOp",EDGE,"E6.26.1.2"),sQuery(id+"F0.wireOp",EDGE,"E6.26.1.3"),sQuery(id+"F0.wireOp",EDGE,"E6.27.0.0"),sQuery(id+"F0.wireOp",EDGE,"E6.27.0.1"),sQuery(id+"F0.wireOp",EDGE,"E6.27.0.2"),sQuery(id+"F0.wireOp",EDGE,"E6.27.0.3"),sQuery(id+"F0.wireOp",EDGE,"E6.27.1.0"),sQuery(id+"F0.wireOp",EDGE,"E6.27.1.1"),sQuery(id+"F0.wireOp",EDGE,"E6.27.1.2"),sQuery(id+"F0.wireOp",EDGE,"E6.27.1.3"),sQuery(id+"F0.wireOp",EDGE,"E6.28.0.0"),sQuery(id+"F0.wireOp",EDGE,"E6.28.0.1"),sQuery(id+"F0.wireOp",EDGE,"E6.28.0.2"),sQuery(id+"F0.wireOp",EDGE,"E6.28.0.3"),sQuery(id+"F0.wireOp",EDGE,"E6.28.1.0"),sQuery(id+"F0.wireOp",EDGE,"E6.28.1.1"),sQuery(id+"F0.wireOp",EDGE,"E6.28.1.2"),sQuery(id+"F0.wireOp",EDGE,"E6.28.1.3"),sQuery(id+"F0.wireOp",EDGE,"E6.29.0.0"),sQuery(id+"F0.wireOp",EDGE,"E6.29.0.1"),sQuery(id+"F0.wireOp",EDGE,"E6.29.0.2"),sQuery(id+"F0.wireOp",EDGE,"E6.29.1.0"),sQuery(id+"F0.wireOp",EDGE,"E6.29.1.1"),sQuery(id+"F0.wireOp",EDGE,"E6.29.1.2"),sQuery(id+"F0.wireOp",EDGE,"E6.29.1.3"),sQuery(id+"F0.wireOp",EDGE,"E7")])]});
            var Q1;
            Q1=makeQuery(id+"F1.opExtrude","SWEPT_FACE",FACE,{"disambiguationData":[OSD([sQuery(id+"F0.wireOp",EDGE,"E0.left")])]});
            mirror(context, id + "F2", {"entities" : qUnion([Q0]), "mirrorPlane" : qUnion([Q1])});
        }
        {
            var Q0;
            Q0=makeQuery(id+"F1.opExtrude","SWEPT_BODY",BODY,{"disambiguationData":[OSD([sQuery(id+"F0.wireOp",EDGE,"E0.bottom"),sQuery(id+"F0.wireOp",EDGE,"E0.top"),sQuery(id+"F0.wireOp",EDGE,"E0.left"),sQuery(id+"F0.wireOp",EDGE,"E0.right"),sQuery(id+"F0.wireOp",EDGE,"E1"),sQuery(id+"F0.wireOp",EDGE,"E3"),sQuery(id+"F0.wireOp",EDGE,"E4"),sQuery(id+"F0.wireOp",EDGE,"E5"),sQuery(id+"F0.wireOp",EDGE,"E6.0.1.0"),sQuery(id+"F0.wireOp",EDGE,"E6.0.1.1"),sQuery(id+"F0.wireOp",EDGE,"E6.0.1.2"),sQuery(id+"F0.wireOp",EDGE,"E6.0.1.3"),sQuery(id+"F0.wireOp",EDGE,"E6.1.0.0"),sQuery(id+"F0.wireOp",EDGE,"E6.1.0.1"),sQuery(id+"F0.wireOp",EDGE,"E6.1.0.2"),sQuery(id+"F0.wireOp",EDGE,"E6.1.0.3"),sQuery(id+"F0.wireOp",EDGE,"E6.1.1.0"),sQuery(id+"F0.wireOp",EDGE,"E6.1.1.1"),sQuery(id+"F0.wireOp",EDGE,"E6.1.1.2"),sQuery(id+"F0.wireOp",EDGE,"E6.1.1.3"),sQuery(id+"F0.wireOp",EDGE,"E6.2.0.0"),sQuery(id+"F0.wireOp",EDGE,"E6.2.0.1"),sQuery(id+"F0.wireOp",EDGE,"E6.2.0.2"),sQuery(id+"F0.wireOp",EDGE,"E6.2.0.3"),sQuery(id+"F0.wireOp",EDGE,"E6.2.1.0"),sQuery(id+"F0.wireOp",EDGE,"E6.2.1.1"),sQuery(id+"F0.wireOp",EDGE,"E6.2.1.2"),sQuery(id+"F0.wireOp",EDGE,"E6.2.1.3"),sQuery(id+"F0.wireOp",EDGE,"E6.3.0.0"),sQuery(id+"F0.wireOp",EDGE,"E6.3.0.1"),sQuery(id+"F0.wireOp",EDGE,"E6.3.0.2"),sQuery(id+"F0.wireOp",EDGE,"E6.3.0.3"),sQuery(id+"F0.wireOp",EDGE,"E6.3.1.0"),sQuery(id+"F0.wireOp",EDGE,"E6.3.1.1"),sQuery(id+"F0.wireOp",EDGE,"E6.3.1.2"),sQuery(id+"F0.wireOp",EDGE,"E6.3.1.3"),sQuery(id+"F0.wireOp",EDGE,"E6.4.0.0"),sQuery(id+"F0.wireOp",EDGE,"E6.4.0.1"),sQuery(id+"F0.wireOp",EDGE,"E6.4.0.2"),sQuery(id+"F0.wireOp",EDGE,"E6.4.0.3"),sQuery(id+"F0.wireOp",EDGE,"E6.4.1.0"),sQuery(id+"F0.wireOp",EDGE,"E6.4.1.1"),sQuery(id+"F0.wireOp",EDGE,"E6.4.1.2"),sQuery(id+"F0.wireOp",EDGE,"E6.4.1.3"),sQuery(id+"F0.wireOp",EDGE,"E6.5.0.0"),sQuery(id+"F0.wireOp",EDGE,"E6.5.0.1"),sQuery(id+"F0.wireOp",EDGE,"E6.5.0.2"),sQuery(id+"F0.wireOp",EDGE,"E6.5.0.3"),sQuery(id+"F0.wireOp",EDGE,"E6.5.1.0"),sQuery(id+"F0.wireOp",EDGE,"E6.5.1.1"),sQuery(id+"F0.wireOp",EDGE,"E6.5.1.2"),sQuery(id+"F0.wireOp",EDGE,"E6.5.1.3"),sQuery(id+"F0.wireOp",EDGE,"E6.6.0.0"),sQuery(id+"F0.wireOp",EDGE,"E6.6.0.1"),sQuery(id+"F0.wireOp",EDGE,"E6.6.0.2"),sQuery(id+"F0.wireOp",EDGE,"E6.6.0.3"),sQuery(id+"F0.wireOp",EDGE,"E6.6.1.0"),sQuery(id+"F0.wireOp",EDGE,"E6.6.1.1"),sQuery(id+"F0.wireOp",EDGE,"E6.6.1.2"),sQuery(id+"F0.wireOp",EDGE,"E6.6.1.3"),sQuery(id+"F0.wireOp",EDGE,"E6.7.0.0"),sQuery(id+"F0.wireOp",EDGE,"E6.7.0.3"),sQuery(id+"F0.wireOp",EDGE,"E6.7.1.0"),sQuery(id+"F0.wireOp",EDGE,"E6.7.1.1"),sQuery(id+"F0.wireOp",EDGE,"E6.7.1.2"),sQuery(id+"F0.wireOp",EDGE,"E6.7.1.3"),sQuery(id+"F0.wireOp",EDGE,"E6.8.0.0"),sQuery(id+"F0.wireOp",EDGE,"E6.8.0.1"),sQuery(id+"F0.wireOp",EDGE,"E6.8.0.2"),sQuery(id+"F0.wireOp",EDGE,"E6.8.0.3"),sQuery(id+"F0.wireOp",EDGE,"E6.8.1.0"),sQuery(id+"F0.wireOp",EDGE,"E6.8.1.1"),sQuery(id+"F0.wireOp",EDGE,"E6.8.1.2"),sQuery(id+"F0.wireOp",EDGE,"E6.8.1.3"),sQuery(id+"F0.wireOp",EDGE,"E6.9.0.0"),sQuery(id+"F0.wireOp",EDGE,"E6.9.0.1"),sQuery(id+"F0.wireOp",EDGE,"E6.9.0.2"),sQuery(id+"F0.wireOp",EDGE,"E6.9.0.3"),sQuery(id+"F0.wireOp",EDGE,"E6.9.1.0"),sQuery(id+"F0.wireOp",EDGE,"E6.9.1.1"),sQuery(id+"F0.wireOp",EDGE,"E6.9.1.2"),sQuery(id+"F0.wireOp",EDGE,"E6.9.1.3"),sQuery(id+"F0.wireOp",EDGE,"E6.10.0.0"),sQuery(id+"F0.wireOp",EDGE,"E6.10.0.1"),sQuery(id+"F0.wireOp",EDGE,"E6.10.0.2"),sQuery(id+"F0.wireOp",EDGE,"E6.10.0.3"),sQuery(id+"F0.wireOp",EDGE,"E6.10.1.0"),sQuery(id+"F0.wireOp",EDGE,"E6.10.1.1"),sQuery(id+"F0.wireOp",EDGE,"E6.10.1.2"),sQuery(id+"F0.wireOp",EDGE,"E6.10.1.3"),sQuery(id+"F0.wireOp",EDGE,"E6.11.0.0"),sQuery(id+"F0.wireOp",EDGE,"E6.11.0.1"),sQuery(id+"F0.wireOp",EDGE,"E6.11.0.2"),sQuery(id+"F0.wireOp",EDGE,"E6.11.0.3"),sQuery(id+"F0.wireOp",EDGE,"E6.11.1.0"),sQuery(id+"F0.wireOp",EDGE,"E6.11.1.1"),sQuery(id+"F0.wireOp",EDGE,"E6.11.1.2"),sQuery(id+"F0.wireOp",EDGE,"E6.11.1.3"),sQuery(id+"F0.wireOp",EDGE,"E6.12.0.0"),sQuery(id+"F0.wireOp",EDGE,"E6.12.0.1"),sQuery(id+"F0.wireOp",EDGE,"E6.12.0.2"),sQuery(id+"F0.wireOp",EDGE,"E6.12.0.3"),sQuery(id+"F0.wireOp",EDGE,"E6.12.1.0"),sQuery(id+"F0.wireOp",EDGE,"E6.12.1.1"),sQuery(id+"F0.wireOp",EDGE,"E6.12.1.2"),sQuery(id+"F0.wireOp",EDGE,"E6.12.1.3"),sQuery(id+"F0.wireOp",EDGE,"E6.13.0.0"),sQuery(id+"F0.wireOp",EDGE,"E6.13.0.1"),sQuery(id+"F0.wireOp",EDGE,"E6.13.0.2"),sQuery(id+"F0.wireOp",EDGE,"E6.13.0.3"),sQuery(id+"F0.wireOp",EDGE,"E6.13.1.0"),sQuery(id+"F0.wireOp",EDGE,"E6.13.1.1"),sQuery(id+"F0.wireOp",EDGE,"E6.13.1.2"),sQuery(id+"F0.wireOp",EDGE,"E6.13.1.3"),sQuery(id+"F0.wireOp",EDGE,"E6.14.0.0"),sQuery(id+"F0.wireOp",EDGE,"E6.14.0.1"),sQuery(id+"F0.wireOp",EDGE,"E6.14.0.2"),sQuery(id+"F0.wireOp",EDGE,"E6.14.0.3"),sQuery(id+"F0.wireOp",EDGE,"E6.14.1.0"),sQuery(id+"F0.wireOp",EDGE,"E6.14.1.1"),sQuery(id+"F0.wireOp",EDGE,"E6.14.1.2"),sQuery(id+"F0.wireOp",EDGE,"E6.14.1.3"),sQuery(id+"F0.wireOp",EDGE,"E6.15.0.0"),sQuery(id+"F0.wireOp",EDGE,"E6.15.0.1"),sQuery(id+"F0.wireOp",EDGE,"E6.15.0.2"),sQuery(id+"F0.wireOp",EDGE,"E6.15.0.3"),sQuery(id+"F0.wireOp",EDGE,"E6.15.1.0"),sQuery(id+"F0.wireOp",EDGE,"E6.15.1.1"),sQuery(id+"F0.wireOp",EDGE,"E6.15.1.2"),sQuery(id+"F0.wireOp",EDGE,"E6.15.1.3"),sQuery(id+"F0.wireOp",EDGE,"E6.16.0.0"),sQuery(id+"F0.wireOp",EDGE,"E6.16.0.1"),sQuery(id+"F0.wireOp",EDGE,"E6.16.0.2"),sQuery(id+"F0.wireOp",EDGE,"E6.16.0.3"),sQuery(id+"F0.wireOp",EDGE,"E6.16.1.0"),sQuery(id+"F0.wireOp",EDGE,"E6.16.1.1"),sQuery(id+"F0.wireOp",EDGE,"E6.16.1.2"),sQuery(id+"F0.wireOp",EDGE,"E6.16.1.3"),sQuery(id+"F0.wireOp",EDGE,"E6.17.0.0"),sQuery(id+"F0.wireOp",EDGE,"E6.17.0.1"),sQuery(id+"F0.wireOp",EDGE,"E6.17.0.2"),sQuery(id+"F0.wireOp",EDGE,"E6.17.0.3"),sQuery(id+"F0.wireOp",EDGE,"E6.17.1.0"),sQuery(id+"F0.wireOp",EDGE,"E6.17.1.1"),sQuery(id+"F0.wireOp",EDGE,"E6.17.1.2"),sQuery(id+"F0.wireOp",EDGE,"E6.17.1.3"),sQuery(id+"F0.wireOp",EDGE,"E6.18.0.0"),sQuery(id+"F0.wireOp",EDGE,"E6.18.0.1"),sQuery(id+"F0.wireOp",EDGE,"E6.18.0.2"),sQuery(id+"F0.wireOp",EDGE,"E6.18.0.3"),sQuery(id+"F0.wireOp",EDGE,"E6.18.1.0"),sQuery(id+"F0.wireOp",EDGE,"E6.18.1.1"),sQuery(id+"F0.wireOp",EDGE,"E6.18.1.2"),sQuery(id+"F0.wireOp",EDGE,"E6.18.1.3"),sQuery(id+"F0.wireOp",EDGE,"E6.19.0.0"),sQuery(id+"F0.wireOp",EDGE,"E6.19.0.1"),sQuery(id+"F0.wireOp",EDGE,"E6.19.0.2"),sQuery(id+"F0.wireOp",EDGE,"E6.19.0.3"),sQuery(id+"F0.wireOp",EDGE,"E6.19.1.0"),sQuery(id+"F0.wireOp",EDGE,"E6.19.1.1"),sQuery(id+"F0.wireOp",EDGE,"E6.19.1.2"),sQuery(id+"F0.wireOp",EDGE,"E6.19.1.3"),sQuery(id+"F0.wireOp",EDGE,"E6.20.0.0"),sQuery(id+"F0.wireOp",EDGE,"E6.20.0.1"),sQuery(id+"F0.wireOp",EDGE,"E6.20.0.2"),sQuery(id+"F0.wireOp",EDGE,"E6.20.0.3"),sQuery(id+"F0.wireOp",EDGE,"E6.20.1.0"),sQuery(id+"F0.wireOp",EDGE,"E6.20.1.1"),sQuery(id+"F0.wireOp",EDGE,"E6.20.1.2"),sQuery(id+"F0.wireOp",EDGE,"E6.20.1.3"),sQuery(id+"F0.wireOp",EDGE,"E6.21.0.0"),sQuery(id+"F0.wireOp",EDGE,"E6.21.0.1"),sQuery(id+"F0.wireOp",EDGE,"E6.21.0.2"),sQuery(id+"F0.wireOp",EDGE,"E6.21.0.3"),sQuery(id+"F0.wireOp",EDGE,"E6.21.1.0"),sQuery(id+"F0.wireOp",EDGE,"E6.21.1.1"),sQuery(id+"F0.wireOp",EDGE,"E6.21.1.2"),sQuery(id+"F0.wireOp",EDGE,"E6.21.1.3"),sQuery(id+"F0.wireOp",EDGE,"E6.22.0.0"),sQuery(id+"F0.wireOp",EDGE,"E6.22.0.1"),sQuery(id+"F0.wireOp",EDGE,"E6.22.0.2"),sQuery(id+"F0.wireOp",EDGE,"E6.22.0.3"),sQuery(id+"F0.wireOp",EDGE,"E6.22.1.0"),sQuery(id+"F0.wireOp",EDGE,"E6.22.1.1"),sQuery(id+"F0.wireOp",EDGE,"E6.22.1.2"),sQuery(id+"F0.wireOp",EDGE,"E6.22.1.3"),sQuery(id+"F0.wireOp",EDGE,"E6.23.0.0"),sQuery(id+"F0.wireOp",EDGE,"E6.23.0.1"),sQuery(id+"F0.wireOp",EDGE,"E6.23.0.2"),sQuery(id+"F0.wireOp",EDGE,"E6.23.0.3"),sQuery(id+"F0.wireOp",EDGE,"E6.23.1.0"),sQuery(id+"F0.wireOp",EDGE,"E6.23.1.1"),sQuery(id+"F0.wireOp",EDGE,"E6.23.1.2"),sQuery(id+"F0.wireOp",EDGE,"E6.23.1.3"),sQuery(id+"F0.wireOp",EDGE,"E6.24.0.0"),sQuery(id+"F0.wireOp",EDGE,"E6.24.0.1"),sQuery(id+"F0.wireOp",EDGE,"E6.24.0.2"),sQuery(id+"F0.wireOp",EDGE,"E6.24.0.3"),sQuery(id+"F0.wireOp",EDGE,"E6.24.1.0"),sQuery(id+"F0.wireOp",EDGE,"E6.24.1.1"),sQuery(id+"F0.wireOp",EDGE,"E6.24.1.2"),sQuery(id+"F0.wireOp",EDGE,"E6.24.1.3"),sQuery(id+"F0.wireOp",EDGE,"E6.25.0.0"),sQuery(id+"F0.wireOp",EDGE,"E6.25.0.1"),sQuery(id+"F0.wireOp",EDGE,"E6.25.0.2"),sQuery(id+"F0.wireOp",EDGE,"E6.25.0.3"),sQuery(id+"F0.wireOp",EDGE,"E6.25.1.0"),sQuery(id+"F0.wireOp",EDGE,"E6.25.1.1"),sQuery(id+"F0.wireOp",EDGE,"E6.25.1.2"),sQuery(id+"F0.wireOp",EDGE,"E6.25.1.3"),sQuery(id+"F0.wireOp",EDGE,"E6.26.0.0"),sQuery(id+"F0.wireOp",EDGE,"E6.26.0.1"),sQuery(id+"F0.wireOp",EDGE,"E6.26.0.2"),sQuery(id+"F0.wireOp",EDGE,"E6.26.0.3"),sQuery(id+"F0.wireOp",EDGE,"E6.26.1.0"),sQuery(id+"F0.wireOp",EDGE,"E6.26.1.1"),sQuery(id+"F0.wireOp",EDGE,"E6.26.1.2"),sQuery(id+"F0.wireOp",EDGE,"E6.26.1.3"),sQuery(id+"F0.wireOp",EDGE,"E6.27.0.0"),sQuery(id+"F0.wireOp",EDGE,"E6.27.0.1"),sQuery(id+"F0.wireOp",EDGE,"E6.27.0.2"),sQuery(id+"F0.wireOp",EDGE,"E6.27.0.3"),sQuery(id+"F0.wireOp",EDGE,"E6.27.1.0"),sQuery(id+"F0.wireOp",EDGE,"E6.27.1.1"),sQuery(id+"F0.wireOp",EDGE,"E6.27.1.2"),sQuery(id+"F0.wireOp",EDGE,"E6.27.1.3"),sQuery(id+"F0.wireOp",EDGE,"E6.28.0.0"),sQuery(id+"F0.wireOp",EDGE,"E6.28.0.1"),sQuery(id+"F0.wireOp",EDGE,"E6.28.0.2"),sQuery(id+"F0.wireOp",EDGE,"E6.28.0.3"),sQuery(id+"F0.wireOp",EDGE,"E6.28.1.0"),sQuery(id+"F0.wireOp",EDGE,"E6.28.1.1"),sQuery(id+"F0.wireOp",EDGE,"E6.28.1.2"),sQuery(id+"F0.wireOp",EDGE,"E6.28.1.3"),sQuery(id+"F0.wireOp",EDGE,"E6.29.0.0"),sQuery(id+"F0.wireOp",EDGE,"E6.29.0.1"),sQuery(id+"F0.wireOp",EDGE,"E6.29.0.2"),sQuery(id+"F0.wireOp",EDGE,"E6.29.1.0"),sQuery(id+"F0.wireOp",EDGE,"E6.29.1.1"),sQuery(id+"F0.wireOp",EDGE,"E6.29.1.2"),sQuery(id+"F0.wireOp",EDGE,"E6.29.1.3"),sQuery(id+"F0.wireOp",EDGE,"E7")])]});
            deleteBodies(context, id + "F3", {"entities" : qUnion([Q0])});
        }
    });
